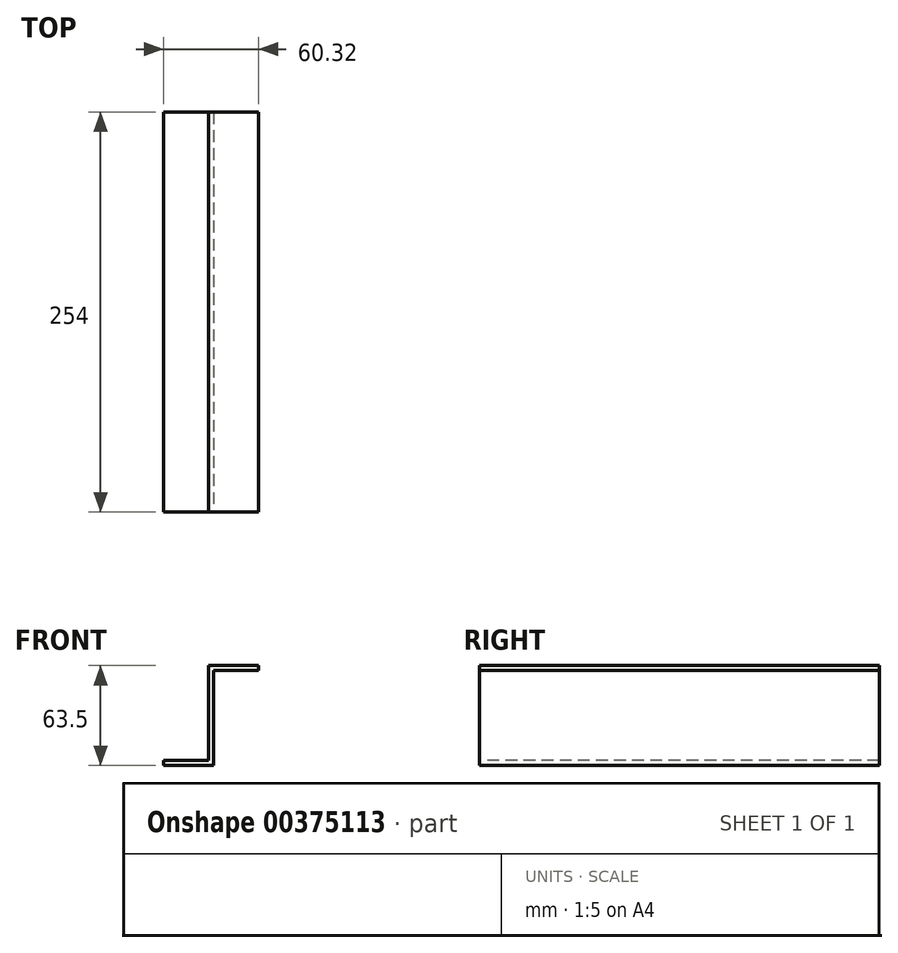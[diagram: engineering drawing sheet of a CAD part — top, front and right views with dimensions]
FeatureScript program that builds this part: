
annotation { "Feature Type Name" : "Feature", "Feature Type Description" : "" }
export const myFeature = defineFeature(function(context is Context, id is Id, definition is map)
    precondition{}
    {
        {
            var Q0;
            Q0=qCreatedBy(makeId("Front.planeOp"),FACE);
            var sketch = newSketch(context, id + "F0", { "sketchPlane" : qUnion([Q0])});
            skLineSegment(sketch, "E0", {"start": v(0, 0) * mm, "end": v(31.75, 0) * mm});
            skLineSegment(sketch, "E1", {"start": v(31.75, 0) * mm, "end": v(31.75, 60.32) * mm});
            skLineSegment(sketch, "E2", {"start": v(31.75, 60.32) * mm, "end": v(60.32, 60.33) * mm});
            skLineSegment(sketch, "E3", {"start": v(60.32, 60.33) * mm, "end": v(60.32, 63.5) * mm});
            skLineSegment(sketch, "E4", {"start": v(60.32, 63.5) * mm, "end": v(28.57, 63.5) * mm});
            skLineSegment(sketch, "E5", {"start": v(28.57, 63.5) * mm, "end": v(28.57, 3.18) * mm});
            skLineSegment(sketch, "E6", {"start": v(28.57, 3.18) * mm, "end": v(0, 3.18) * mm});
            skLineSegment(sketch, "E7", {"start": v(0, 3.18) * mm, "end": v(0, 0) * mm});
            skSolve(sketch);
        }
        {
            var Q0;
            Q0=makeQuery(id+"F0.imprint","IMPRINT",FACE,{"disambiguationData":[TD([[makeQuery(id+"F0.imprint","IMPRINT",EDGE,{"derivedFrom":sQuery(id+"F0.wireOp",EDGE,"E0")}),1.0]])]});
            extrude(context, id + "F1", {"entities" : qUnion([Q0]), "oppositeDirection" : true, "depth" : 254 * mm});
        }
    });
